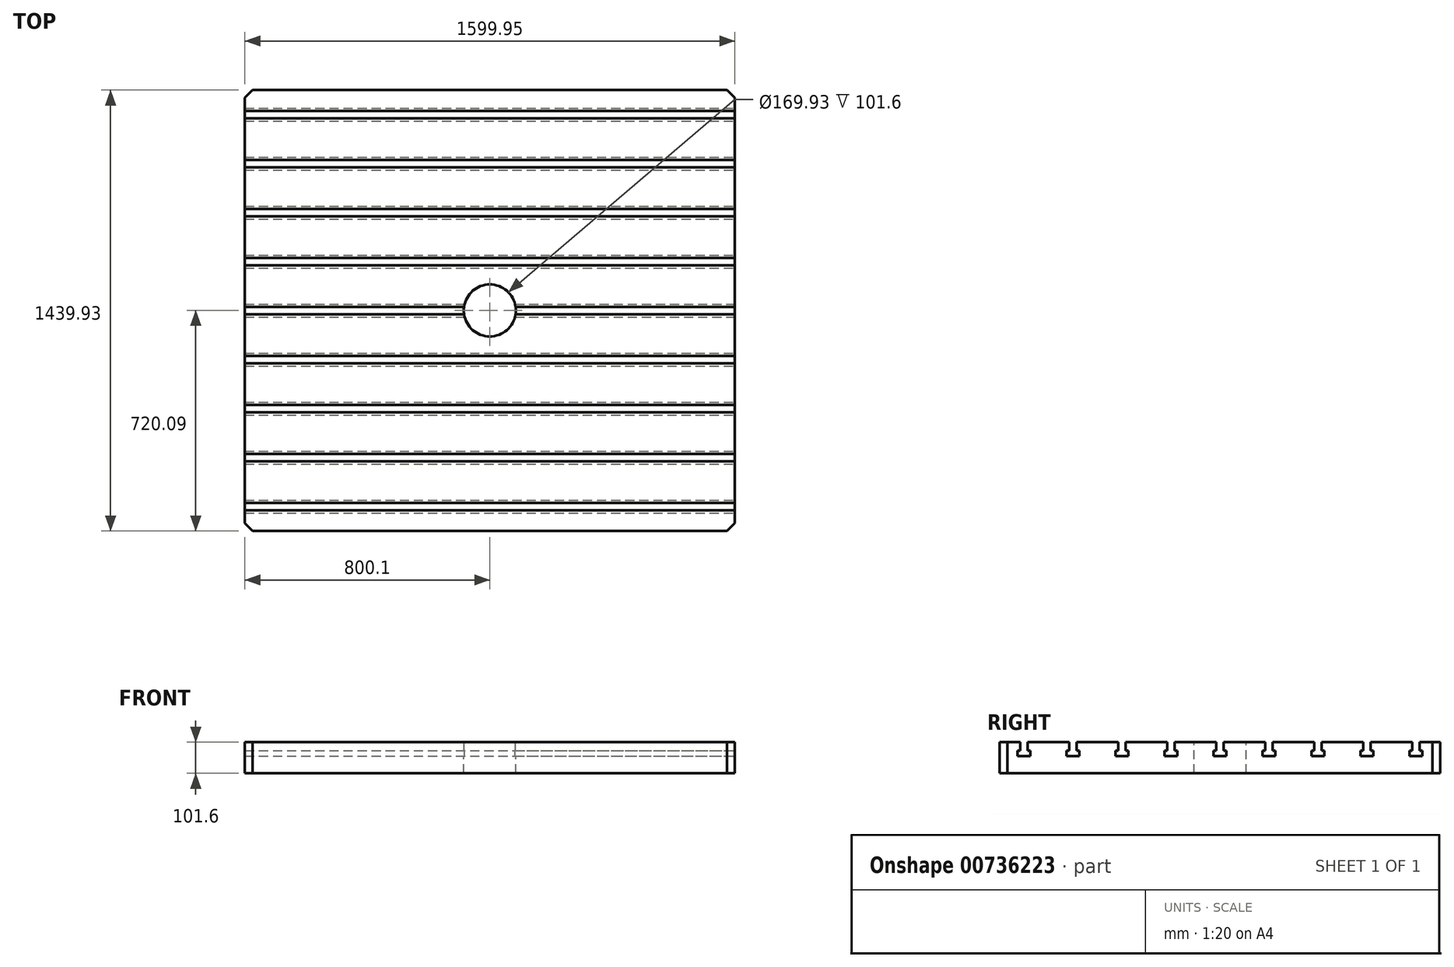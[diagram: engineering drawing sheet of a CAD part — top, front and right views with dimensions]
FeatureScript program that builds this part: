
annotation { "Feature Type Name" : "Feature", "Feature Type Description" : "" }
export const myFeature = defineFeature(function(context is Context, id is Id, definition is map)
    precondition{}
    {
        {
            var Q0;
            Q0=qCreatedBy(makeId("Top.planeOp"),FACE);
            var sketch = newSketch(context, id + "F0", { "sketchPlane" : qUnion([Q0])});
            skLineSegment(sketch, "E0.bottom", {"start": v(0, 0) * mm, "end": v(1599.95, 0) * mm});
            skLineSegment(sketch, "E0.top", {"start": v(0, 1439.93) * mm, "end": v(1599.95, 1439.93) * mm});
            skLineSegment(sketch, "E0.left", {"start": v(0, 0) * mm, "end": v(0, 1439.93) * mm});
            skLineSegment(sketch, "E0.right", {"start": v(1599.95, 0) * mm, "end": v(1599.95, 1439.93) * mm});
            skSolve(sketch);
        }
        {
            var Q0;
            Q0=makeQuery(id+"F0.imprint","IMPRINT",FACE,{"disambiguationData":[TD([[makeQuery(id+"F0.imprint","IMPRINT",EDGE,{"derivedFrom":sQuery(id+"F0.wireOp",EDGE,"E0.bottom")}),1.0]])]});
            extrude(context, id + "F1", {"entities" : qUnion([Q0]), "oppositeDirection" : true, "depth" : 101.6 * mm, "offsetDistance" : 25.4 * mm});
        }
        {
            var Q0;
            Q0=makeQuery(id+"F1.opExtrude","SWEPT_FACE",FACE,{"disambiguationData":[OSD([sQuery(id+"F0.wireOp",EDGE,"E0.right")])]});
            var sketch = newSketch(context, id + "F2", { "sketchPlane" : qUnion([Q0])});
            skLineSegment(sketch, "E1", {"start": v(68.02, 0) * mm, "end": v(68.02, -27) * mm});
            skLineSegment(sketch, "E2", {"start": v(59, -45) * mm, "end": v(101.01, -45) * mm});
            skLineSegment(sketch, "E3", {"start": v(101.01, -45) * mm, "end": v(101.01, -27) * mm});
            skLineSegment(sketch, "E4", {"start": v(101.01, -27) * mm, "end": v(92, -27) * mm});
            skLineSegment(sketch, "E5", {"start": v(92, -27) * mm, "end": v(92, 0) * mm});
            skLineSegment(sketch, "E6", {"start": v(92, 0) * mm, "end": v(68.02, 0) * mm});
            skLineSegment(sketch, "E7", {"start": v(80, 63.64) * mm, "end": v(80, -155.3) * mm, "construction": true});
            skLineSegment(sketch, "E8", {"start": v(719.96, 82.23) * mm, "end": v(719.96, -270.48) * mm, "construction": true});
            skLineSegment(sketch, "E9.MirrorCS", {"start": v(68.02, 0) * mm, "end": v(92, 0) * mm});
            skLineSegment(sketch, "E10.MirrorCS", {"start": v(59, -45) * mm, "end": v(59, -27) * mm});
            skLineSegment(sketch, "E11.MirrorCS", {"start": v(59, -27) * mm, "end": v(68.02, -27) * mm});
            skLineSegment(sketch, "E12.MirrorCS", {"start": v(68.02, -27) * mm, "end": v(68.02, 0) * mm});
            skLineSegment(sketch, "E13.MirrorCS", {"start": v(92, 0) * mm, "end": v(92, -27) * mm});
            skLineSegment(sketch, "E14.MirrorCS", {"start": v(1371.9, 0) * mm, "end": v(1347.93, 0) * mm});
            skLineSegment(sketch, "E15.MirrorCS", {"start": v(1347.93, 0) * mm, "end": v(1371.9, 0) * mm});
            skLineSegment(sketch, "E16.MirrorCS", {"start": v(1338.92, -27) * mm, "end": v(1347.93, -27) * mm});
            skLineSegment(sketch, "E17.MirrorCS", {"start": v(1380.92, -27) * mm, "end": v(1371.9, -27) * mm});
            skLineSegment(sketch, "E18.MirrorCS", {"start": v(1338.92, -45) * mm, "end": v(1338.92, -27) * mm});
            skLineSegment(sketch, "E19.MirrorCS", {"start": v(1380.92, -45) * mm, "end": v(1380.92, -27) * mm});
            skLineSegment(sketch, "E20.MirrorCS", {"start": v(1347.93, 0) * mm, "end": v(1347.93, -27) * mm});
            skLineSegment(sketch, "E21.MirrorCS", {"start": v(1371.9, -27) * mm, "end": v(1371.9, 0) * mm});
            skLineSegment(sketch, "E22.MirrorCS", {"start": v(1371.9, 0) * mm, "end": v(1371.9, -27) * mm});
            skLineSegment(sketch, "E23.MirrorCS", {"start": v(1359.92, 63.64) * mm, "end": v(1359.92, -155.3) * mm, "construction": true});
            skLineSegment(sketch, "E24.MirrorCS", {"start": v(1347.93, -27) * mm, "end": v(1347.93, 0) * mm});
            skLineSegment(sketch, "E25.MirrorCS", {"start": v(1380.92, -45) * mm, "end": v(1338.92, -45) * mm});
            skLineSegment(sketch, "E26.1.0.0", {"start": v(252.02, -27) * mm, "end": v(252.02, 0) * mm});
            skLineSegment(sketch, "E26.1.0.1", {"start": v(261.03, -27) * mm, "end": v(252.02, -27) * mm});
            skLineSegment(sketch, "E26.1.0.2", {"start": v(261.03, -45) * mm, "end": v(261.03, -27) * mm});
            skLineSegment(sketch, "E26.1.0.3", {"start": v(219.03, -45) * mm, "end": v(261.03, -45) * mm});
            skLineSegment(sketch, "E26.1.0.4", {"start": v(228.04, 0) * mm, "end": v(228.04, -27) * mm});
            skLineSegment(sketch, "E26.1.0.5", {"start": v(219.03, -45) * mm, "end": v(219.03, -27) * mm});
            skLineSegment(sketch, "E26.1.0.6", {"start": v(252.02, 0) * mm, "end": v(228.04, 0) * mm});
            skLineSegment(sketch, "E26.1.0.7", {"start": v(219.03, -27) * mm, "end": v(228.04, -27) * mm});
            skLineSegment(sketch, "E26.1.0.8", {"start": v(228.04, -27) * mm, "end": v(228.04, 0) * mm});
            skLineSegment(sketch, "E26.1.0.9", {"start": v(252.02, 0) * mm, "end": v(252.02, -27) * mm});
            skLineSegment(sketch, "E26.1.0.10", {"start": v(228.04, 0) * mm, "end": v(252.02, 0) * mm});
            skLineSegment(sketch, "E26.2.0.0", {"start": v(412.04, -27) * mm, "end": v(412.04, 0) * mm});
            skLineSegment(sketch, "E26.2.0.1", {"start": v(421.05, -27) * mm, "end": v(412.04, -27) * mm});
            skLineSegment(sketch, "E26.2.0.2", {"start": v(421.05, -45) * mm, "end": v(421.05, -27) * mm});
            skLineSegment(sketch, "E26.2.0.3", {"start": v(379.05, -45) * mm, "end": v(421.05, -45) * mm});
            skLineSegment(sketch, "E26.2.0.4", {"start": v(388.06, 0) * mm, "end": v(388.06, -27) * mm});
            skLineSegment(sketch, "E26.2.0.5", {"start": v(379.05, -45) * mm, "end": v(379.05, -27) * mm});
            skLineSegment(sketch, "E26.2.0.6", {"start": v(412.04, 0) * mm, "end": v(388.06, 0) * mm});
            skLineSegment(sketch, "E26.2.0.7", {"start": v(379.05, -27) * mm, "end": v(388.06, -27) * mm});
            skLineSegment(sketch, "E26.2.0.8", {"start": v(388.06, -27) * mm, "end": v(388.06, 0) * mm});
            skLineSegment(sketch, "E26.2.0.9", {"start": v(412.04, 0) * mm, "end": v(412.04, -27) * mm});
            skLineSegment(sketch, "E26.2.0.10", {"start": v(388.06, 0) * mm, "end": v(412.04, 0) * mm});
            skLineSegment(sketch, "E26.3.0.0", {"start": v(572.06, -27) * mm, "end": v(572.06, 0) * mm});
            skLineSegment(sketch, "E26.3.0.1", {"start": v(581.07, -27) * mm, "end": v(572.06, -27) * mm});
            skLineSegment(sketch, "E26.3.0.2", {"start": v(581.07, -45) * mm, "end": v(581.07, -27) * mm});
            skLineSegment(sketch, "E26.3.0.3", {"start": v(539.07, -45) * mm, "end": v(581.07, -45) * mm});
            skLineSegment(sketch, "E26.3.0.4", {"start": v(548.08, 0) * mm, "end": v(548.08, -27) * mm});
            skLineSegment(sketch, "E26.3.0.5", {"start": v(539.07, -45) * mm, "end": v(539.07, -27) * mm});
            skLineSegment(sketch, "E26.3.0.6", {"start": v(572.06, 0) * mm, "end": v(548.08, 0) * mm});
            skLineSegment(sketch, "E26.3.0.7", {"start": v(539.07, -27) * mm, "end": v(548.08, -27) * mm});
            skLineSegment(sketch, "E26.3.0.8", {"start": v(548.08, -27) * mm, "end": v(548.08, 0) * mm});
            skLineSegment(sketch, "E26.3.0.9", {"start": v(572.06, 0) * mm, "end": v(572.06, -27) * mm});
            skLineSegment(sketch, "E26.3.0.10", {"start": v(548.08, 0) * mm, "end": v(572.06, 0) * mm});
            skLineSegment(sketch, "E26.4.0.0", {"start": v(732.08, -27) * mm, "end": v(732.08, 0) * mm});
            skLineSegment(sketch, "E26.4.0.1", {"start": v(741.1, -27) * mm, "end": v(732.08, -27) * mm});
            skLineSegment(sketch, "E26.4.0.2", {"start": v(741.1, -45) * mm, "end": v(741.1, -27) * mm});
            skLineSegment(sketch, "E26.4.0.3", {"start": v(699.09, -45) * mm, "end": v(741.1, -45) * mm});
            skLineSegment(sketch, "E26.4.0.4", {"start": v(708.1, 0) * mm, "end": v(708.1, -27) * mm});
            skLineSegment(sketch, "E26.4.0.5", {"start": v(699.1, -45) * mm, "end": v(699.1, -27) * mm});
            skLineSegment(sketch, "E26.4.0.6", {"start": v(732.08, 0) * mm, "end": v(708.1, 0) * mm});
            skLineSegment(sketch, "E26.4.0.7", {"start": v(699.09, -27) * mm, "end": v(708.1, -27) * mm});
            skLineSegment(sketch, "E26.4.0.8", {"start": v(708.1, -27) * mm, "end": v(708.1, 0) * mm});
            skLineSegment(sketch, "E26.4.0.9", {"start": v(732.08, 0) * mm, "end": v(732.08, -27) * mm});
            skLineSegment(sketch, "E26.4.0.10", {"start": v(708.1, 0) * mm, "end": v(732.08, 0) * mm});
            skLineSegment(sketch, "E26.5.0.0", {"start": v(892.1, -27) * mm, "end": v(892.1, 0) * mm});
            skLineSegment(sketch, "E26.5.0.1", {"start": v(901.11, -27) * mm, "end": v(892.1, -27) * mm});
            skLineSegment(sketch, "E26.5.0.2", {"start": v(901.11, -45) * mm, "end": v(901.11, -27) * mm});
            skLineSegment(sketch, "E26.5.0.3", {"start": v(859.1, -45) * mm, "end": v(901.11, -45) * mm});
            skLineSegment(sketch, "E26.5.0.4", {"start": v(868.12, 0) * mm, "end": v(868.12, -27) * mm});
            skLineSegment(sketch, "E26.5.0.5", {"start": v(859.11, -45) * mm, "end": v(859.11, -27) * mm});
            skLineSegment(sketch, "E26.5.0.6", {"start": v(892.1, 0) * mm, "end": v(868.12, 0) * mm});
            skLineSegment(sketch, "E26.5.0.7", {"start": v(859.1, -27) * mm, "end": v(868.12, -27) * mm});
            skLineSegment(sketch, "E26.5.0.8", {"start": v(868.12, -27) * mm, "end": v(868.12, 0) * mm});
            skLineSegment(sketch, "E26.5.0.9", {"start": v(892.1, 0) * mm, "end": v(892.1, -27) * mm});
            skLineSegment(sketch, "E26.5.0.10", {"start": v(868.12, 0) * mm, "end": v(892.1, 0) * mm});
            skLineSegment(sketch, "E26.6.0.0", {"start": v(1052.12, -27) * mm, "end": v(1052.12, 0) * mm});
            skLineSegment(sketch, "E26.6.0.1", {"start": v(1061.13, -27) * mm, "end": v(1052.12, -27) * mm});
            skLineSegment(sketch, "E26.6.0.2", {"start": v(1061.13, -45) * mm, "end": v(1061.13, -27) * mm});
            skLineSegment(sketch, "E26.6.0.3", {"start": v(1019.13, -45) * mm, "end": v(1061.13, -45) * mm});
            skLineSegment(sketch, "E26.6.0.4", {"start": v(1028.14, 0) * mm, "end": v(1028.14, -27) * mm});
            skLineSegment(sketch, "E26.6.0.5", {"start": v(1019.13, -45) * mm, "end": v(1019.13, -27) * mm});
            skLineSegment(sketch, "E26.6.0.6", {"start": v(1052.12, 0) * mm, "end": v(1028.14, 0) * mm});
            skLineSegment(sketch, "E26.6.0.7", {"start": v(1019.13, -27) * mm, "end": v(1028.14, -27) * mm});
            skLineSegment(sketch, "E26.6.0.8", {"start": v(1028.14, -27) * mm, "end": v(1028.14, 0) * mm});
            skLineSegment(sketch, "E26.6.0.9", {"start": v(1052.12, 0) * mm, "end": v(1052.12, -27) * mm});
            skLineSegment(sketch, "E26.6.0.10", {"start": v(1028.14, 0) * mm, "end": v(1052.12, 0) * mm});
            skLineSegment(sketch, "E26.7.0.0", {"start": v(1212.14, -27) * mm, "end": v(1212.14, 0) * mm});
            skLineSegment(sketch, "E26.7.0.1", {"start": v(1221.15, -27) * mm, "end": v(1212.14, -27) * mm});
            skLineSegment(sketch, "E26.7.0.2", {"start": v(1221.15, -45) * mm, "end": v(1221.15, -27) * mm});
            skLineSegment(sketch, "E26.7.0.3", {"start": v(1179.15, -45) * mm, "end": v(1221.15, -45) * mm});
            skLineSegment(sketch, "E26.7.0.4", {"start": v(1188.16, 0) * mm, "end": v(1188.16, -27) * mm});
            skLineSegment(sketch, "E26.7.0.5", {"start": v(1179.15, -45) * mm, "end": v(1179.15, -27) * mm});
            skLineSegment(sketch, "E26.7.0.6", {"start": v(1212.14, 0) * mm, "end": v(1188.16, 0) * mm});
            skLineSegment(sketch, "E26.7.0.7", {"start": v(1179.15, -27) * mm, "end": v(1188.16, -27) * mm});
            skLineSegment(sketch, "E26.7.0.8", {"start": v(1188.16, -27) * mm, "end": v(1188.16, 0) * mm});
            skLineSegment(sketch, "E26.7.0.9", {"start": v(1212.14, 0) * mm, "end": v(1212.14, -27) * mm});
            skLineSegment(sketch, "E26.7.0.10", {"start": v(1188.16, 0) * mm, "end": v(1212.14, 0) * mm});
            skLineSegment(sketch, "E26.direction1", {"start": v(59, -45) * mm, "end": v(219.03, -45) * mm, "construction": true});
            skSolve(sketch);
        }
        {
            var Q0;
            Q0 = qSketchRegion(id + "F2", true);
            extrude(context, id + "F3", {"entities" : qUnion([Q0]), "operationType" : NewBodyOperationType.REMOVE, "endBound" : BoundingType.THROUGH_ALL, "oppositeDirection" : true, "depth" : 25.4 * mm, "offsetDistance" : 25.4 * mm});
        }
        {
            var Q0;
            Q0=makeQuery(id+"F1.opExtrude","SWEPT_EDGE",EDGE,{"disambiguationData":[OSD([sQuery(id+"F0.wireOp",EDGE,"E0.bottom"),sQuery(id+"F0.wireOp",EDGE,"E0.right")])]});
            var Q1;
            Q1=makeQuery(id+"F1.opExtrude","SWEPT_EDGE",EDGE,{"disambiguationData":[OSD([sQuery(id+"F0.wireOp",EDGE,"E0.top"),sQuery(id+"F0.wireOp",EDGE,"E0.right")])]});
            var Q2;
            Q2=makeQuery(id+"F1.opExtrude","SWEPT_EDGE",EDGE,{"disambiguationData":[OSD([sQuery(id+"F0.wireOp",EDGE,"E0.bottom"),sQuery(id+"F0.wireOp",EDGE,"E0.left")])]});
            var Q3;
            Q3=makeQuery(id+"F1.opExtrude","SWEPT_EDGE",EDGE,{"disambiguationData":[OSD([sQuery(id+"F0.wireOp",EDGE,"E0.top"),sQuery(id+"F0.wireOp",EDGE,"E0.left")])]});
            chamfer(context, id + "F4", {"entities" : qUnion([Q0, Q1, Q2, Q3]), "width" : 25.4 * mm, "tangentPropagation" : true});
        }
        {
            var Q0;
            {var subQ0=sQuery(id+"F0.wireOp",EDGE,"E0.left");var subQ1=sQuery(id+"F0.wireOp",EDGE,"E0.right");Q0=makeQuery(id+"F3.boolean.opBoolean","SPLIT",FACE,{"disambiguationData":[TD([makeQuery(id+"F3.opExtrude","SWEPT_FACE",FACE,{"disambiguationData":[OSD([sQuery(id+"F2.wireOp",EDGE,"E26.4.0.8")])]})])],"derivedFrom":makeQuery(id+"F1.opExtrude","CAP_FACE",FACE,{"disambiguationData":[OSD([sQuery(id+"F0.wireOp",EDGE,"E0.bottom"),sQuery(id+"F0.wireOp",EDGE,"E0.top"),subQ0,subQ1])],"isStart":true})});}
            var sketch = newSketch(context, id + "F5", { "sketchPlane" : qUnion([Q0])});
            skCircle(sketch, "E27", {"center": v(800.1, 720.1) * mm, "radius": 84.96 * mm});
            skSolve(sketch);
        }
        {
            var Q0;
            Q0 = qSketchRegion(id + "F5", true);
            extrude(context, id + "F6", {"entities" : qUnion([Q0]), "operationType" : NewBodyOperationType.REMOVE, "endBound" : BoundingType.THROUGH_ALL, "oppositeDirection" : true, "depth" : 25.4 * mm, "offsetDistance" : 25.4 * mm});
        }
    });
